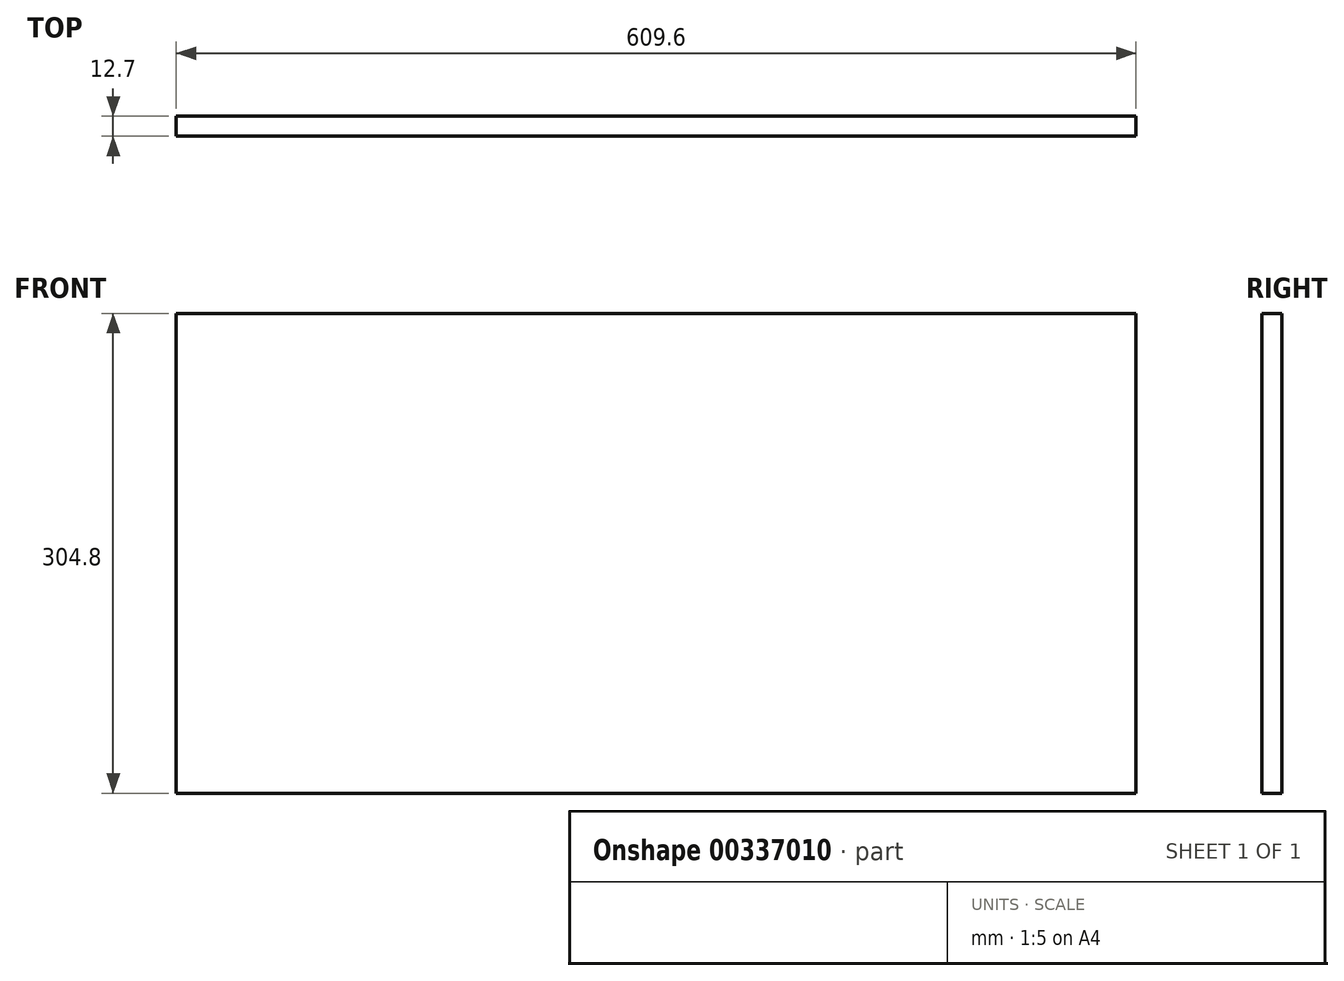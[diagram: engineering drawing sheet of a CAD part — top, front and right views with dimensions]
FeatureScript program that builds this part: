
annotation { "Feature Type Name" : "Feature", "Feature Type Description" : "" }
export const myFeature = defineFeature(function(context is Context, id is Id, definition is map)
    precondition{}
    {
        {
            var Q0;
            Q0=qCreatedBy(makeId("Front.planeOp"),FACE);
            var sketch = newSketch(context, id + "F0", { "sketchPlane" : qUnion([Q0])});
            skLineSegment(sketch, "E0", {"start": v(-315.24, 58.86) * mm, "end": v(294.36, 58.86) * mm});
            skLineSegment(sketch, "E1", {"start": v(294.36, 58.86) * mm, "end": v(294.36, -245.94) * mm});
            skLineSegment(sketch, "E2", {"start": v(294.36, -245.94) * mm, "end": v(-315.24, -245.94) * mm});
            skLineSegment(sketch, "E3", {"start": v(-315.24, -245.94) * mm, "end": v(-315.24, 58.86) * mm});
            skSolve(sketch);
        }
        {
            var Q0;
            Q0 = qSketchRegion(id + "F0", true);
            extrude(context, id + "F1", {"entities" : qUnion([Q0]), "depth" : 12.7 * mm});
        }
    });
